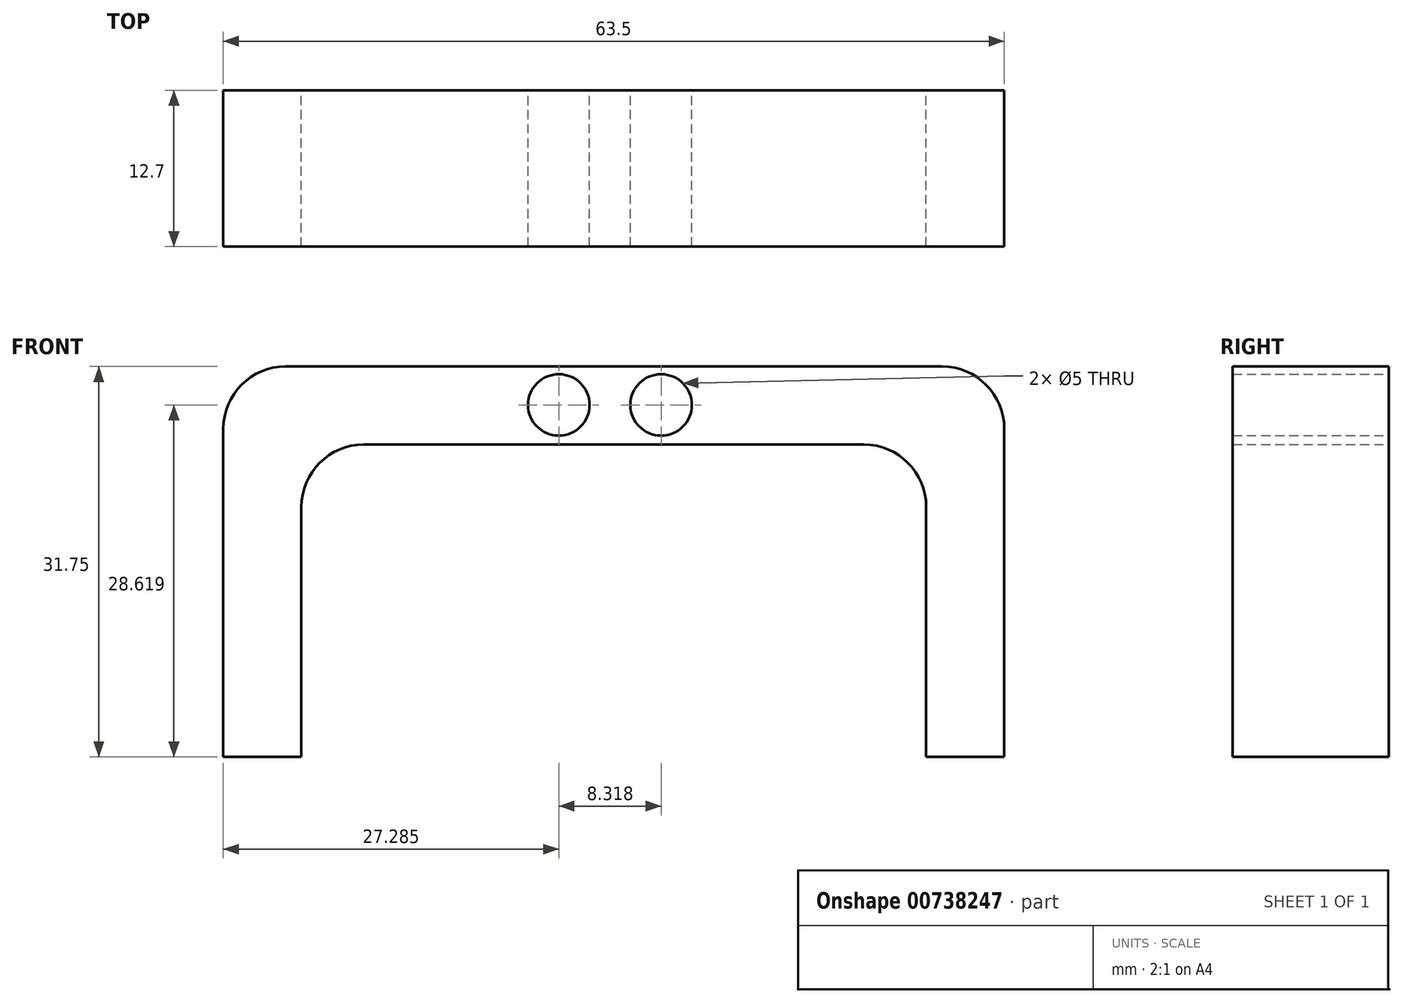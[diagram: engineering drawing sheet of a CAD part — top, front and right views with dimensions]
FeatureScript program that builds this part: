
annotation { "Feature Type Name" : "Feature", "Feature Type Description" : "" }
export const myFeature = defineFeature(function(context is Context, id is Id, definition is map)
    precondition{}
    {
        {
            var Q0;
            Q0=qCreatedBy(makeId("Front.planeOp"),FACE);
            var sketch = newSketch(context, id + "F0", { "sketchPlane" : qUnion([Q0])});
            skLineSegment(sketch, "E0", {"start": v(-17.67, 27.88) * mm, "end": v(45.83, 27.88) * mm});
            skLineSegment(sketch, "E1", {"start": v(-17.67, 27.88) * mm, "end": v(-17.67, -3.87) * mm});
            skLineSegment(sketch, "E2", {"start": v(45.83, 27.88) * mm, "end": v(45.83, -3.87) * mm});
            skLineSegment(sketch, "E3", {"start": v(45.83, -3.87) * mm, "end": v(39.48, -3.87) * mm});
            skLineSegment(sketch, "E4", {"start": v(39.48, -3.87) * mm, "end": v(39.48, 21.53) * mm});
            skLineSegment(sketch, "E5", {"start": v(39.48, 21.53) * mm, "end": v(-11.32, 21.53) * mm});
            skLineSegment(sketch, "E6", {"start": v(-11.32, 21.53) * mm, "end": v(-11.32, -3.87) * mm});
            skLineSegment(sketch, "E7", {"start": v(-11.32, -3.87) * mm, "end": v(-17.67, -3.87) * mm});
            skCircle(sketch, "E8", {"center": v(17.93, 24.75) * mm, "radius": 2.5 * mm});
            skCircle(sketch, "E9", {"center": v(9.61, 24.75) * mm, "radius": 2.5 * mm});
            skSolve(sketch);
        }
        {
            var Q0;
            Q0=makeQuery(id+"F0.imprint","IMPRINT",FACE,{"disambiguationData":[TD([[makeQuery(id+"F0.imprint","IMPRINT",EDGE,{"derivedFrom":sQuery(id+"F0.wireOp",EDGE,"E0")}),-1.0]])]});
            extrude(context, id + "F1", {"entities" : qUnion([Q0]), "depth" : 12.7 * mm, "offsetDistance" : 25.4 * mm});
        }
        {
            var Q0;
            Q0=makeQuery(id+"F1.opExtrude","SWEPT_EDGE",EDGE,{"disambiguationData":[OSD([sQuery(id+"F0.wireOp",EDGE,"E0"),sQuery(id+"F0.wireOp",EDGE,"E1")])]});
            var Q1;
            Q1=makeQuery(id+"F1.opExtrude","SWEPT_EDGE",EDGE,{"disambiguationData":[OSD([sQuery(id+"F0.wireOp",EDGE,"E5"),sQuery(id+"F0.wireOp",EDGE,"E6")])]});
            var Q2;
            Q2=makeQuery(id+"F1.opExtrude","SWEPT_EDGE",EDGE,{"disambiguationData":[OSD([sQuery(id+"F0.wireOp",EDGE,"E0"),sQuery(id+"F0.wireOp",EDGE,"E2")])]});
            var Q3;
            Q3=makeQuery(id+"F1.opExtrude","SWEPT_EDGE",EDGE,{"disambiguationData":[OSD([sQuery(id+"F0.wireOp",EDGE,"E4"),sQuery(id+"F0.wireOp",EDGE,"E5")])]});
            fillet(context, id + "F2", {"entities" : qUnion([Q0, Q1, Q2, Q3]), "radius" : 5.08 * mm, "tangentPropagation" : true, "allowEdgeOverflow" : false});
        }
    });
